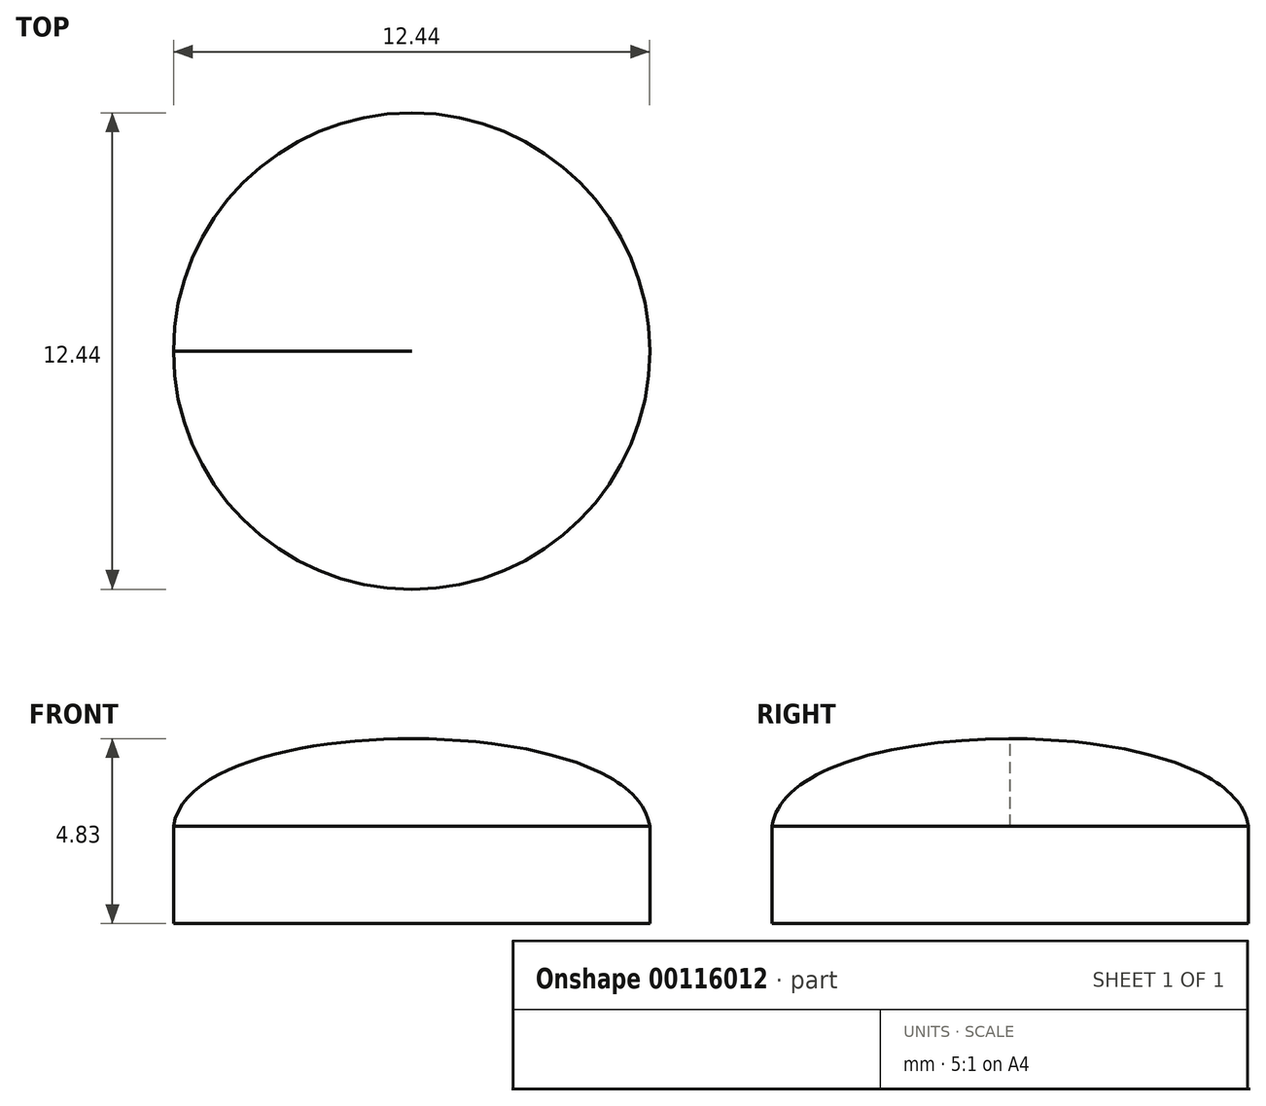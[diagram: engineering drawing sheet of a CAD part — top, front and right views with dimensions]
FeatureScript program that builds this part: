
annotation { "Feature Type Name" : "Feature", "Feature Type Description" : "" }
export const myFeature = defineFeature(function(context is Context, id is Id, definition is map)
    precondition{}
    {
        {
            var Q0;
            Q0=qCreatedBy(makeId("Front.planeOp"),FACE);
            var sketch = newSketch(context, id + "F0", { "sketchPlane" : qUnion([Q0])});
            skLineSegment(sketch, "E0", {"start": v(0, 1.86) * mm, "end": v(0, -2.97) * mm});
            skLineSegment(sketch, "E1", {"start": v(0, -2.97) * mm, "end": v(-6.22, -2.97) * mm});
            skLineSegment(sketch, "E2", {"start": v(-6.22, -2.97) * mm, "end": v(-6.22, -0.43) * mm});
            skFitSpline(sketch, "E3", {"points": [v(-6.22, -0.43) * mm, v(0, 1.86) * mm], "startDerivative": vector(0.72, 4.8) * mm, "endDerivative": vector(8.39, -0.02) * mm});
            skSolve(sketch);
        }
        {
            var Q0;
            Q0 = qSketchRegion(id + "F0", true);
            var Q1;
            Q1=sQuery(id+"F0.wireOp",EDGE,"E0");
            revolve(context, id + "F1", {"entities" : qUnion([Q0]), "axis" : qUnion([Q1]), "revolveType" : RevolveType.FULL});
        }
    });
